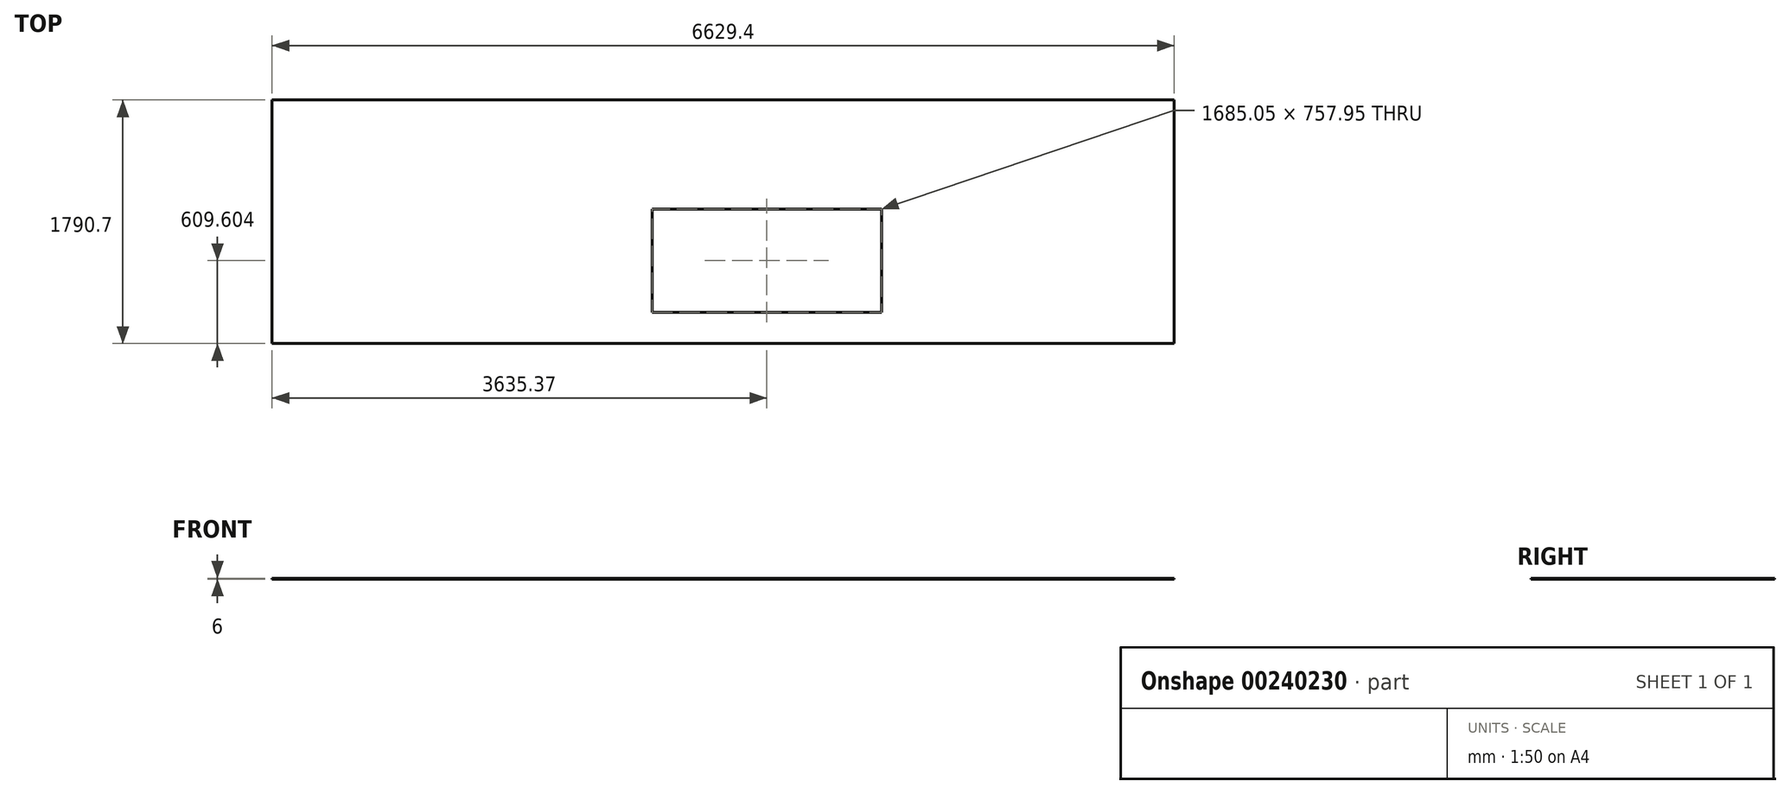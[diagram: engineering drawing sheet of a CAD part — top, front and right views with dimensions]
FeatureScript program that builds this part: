
annotation { "Feature Type Name" : "Feature", "Feature Type Description" : "" }
export const myFeature = defineFeature(function(context is Context, id is Id, definition is map)
    precondition{}
    {
        {
            var Q0;
            Q0=qCreatedBy(makeId("Top.planeOp"),FACE);
            var sketch = newSketch(context, id + "F0", { "sketchPlane" : qUnion([Q0])});
            skLineSegment(sketch, "E0.top", {"start": v(3090.5, 1047.66) * mm, "end": v(-3538.9, 1047.66) * mm});
            skLineSegment(sketch, "E0.left", {"start": v(3090.5, 1047.66) * mm, "end": v(3090.5, 1047.66) * mm});
            skLineSegment(sketch, "E1.top", {"start": v(-3538.9, -743.04) * mm, "end": v(3090.5, -743.04) * mm});
            skLineSegment(sketch, "E2.bottom", {"start": v(-3538.9, 1047.66) * mm, "end": v(3090.5, 1047.66) * mm});
            skLineSegment(sketch, "E2.left", {"start": v(-3538.9, 1047.66) * mm, "end": v(-3538.9, -743.04) * mm});
            skLineSegment(sketch, "E2.right", {"start": v(3090.5, 1047.66) * mm, "end": v(3090.5, -743.04) * mm});
            skLineSegment(sketch, "E3.bottom", {"start": v(-746.05, 245.54) * mm, "end": v(939, 245.54) * mm});
            skLineSegment(sketch, "E3.top", {"start": v(-746.05, -512.41) * mm, "end": v(939, -512.41) * mm});
            skLineSegment(sketch, "E3.left", {"start": v(-746.05, 245.54) * mm, "end": v(-746.05, -512.41) * mm});
            skLineSegment(sketch, "E3.right", {"start": v(939, 245.54) * mm, "end": v(939, -512.41) * mm});
            skLineSegment(sketch, "E4", {"start": v(939, -512.41) * mm, "end": v(-746.05, 245.54) * mm, "construction": true});
            skLineSegment(sketch, "E5", {"start": v(-746.05, -512.41) * mm, "end": v(939, 245.54) * mm, "construction": true});
            skLineSegment(sketch, "E6", {"start": v(96.47, -133.44) * mm, "end": v(96.47, -512.41) * mm, "construction": true});
            skSolve(sketch);
        }
        {
            var Q0;
            Q0=makeQuery(id+"F0.imprint","IMPRINT",FACE,{"disambiguationData":[TD([[makeQuery(id+"F0.imprint","IMPRINT",EDGE,{"derivedFrom":sQuery(id+"F0.wireOp",EDGE,"E1.top")}),1.0]])]});
            extrude(context, id + "F1", {"entities" : qUnion([Q0]), "depth" : 6 * mm});
        }
    });
